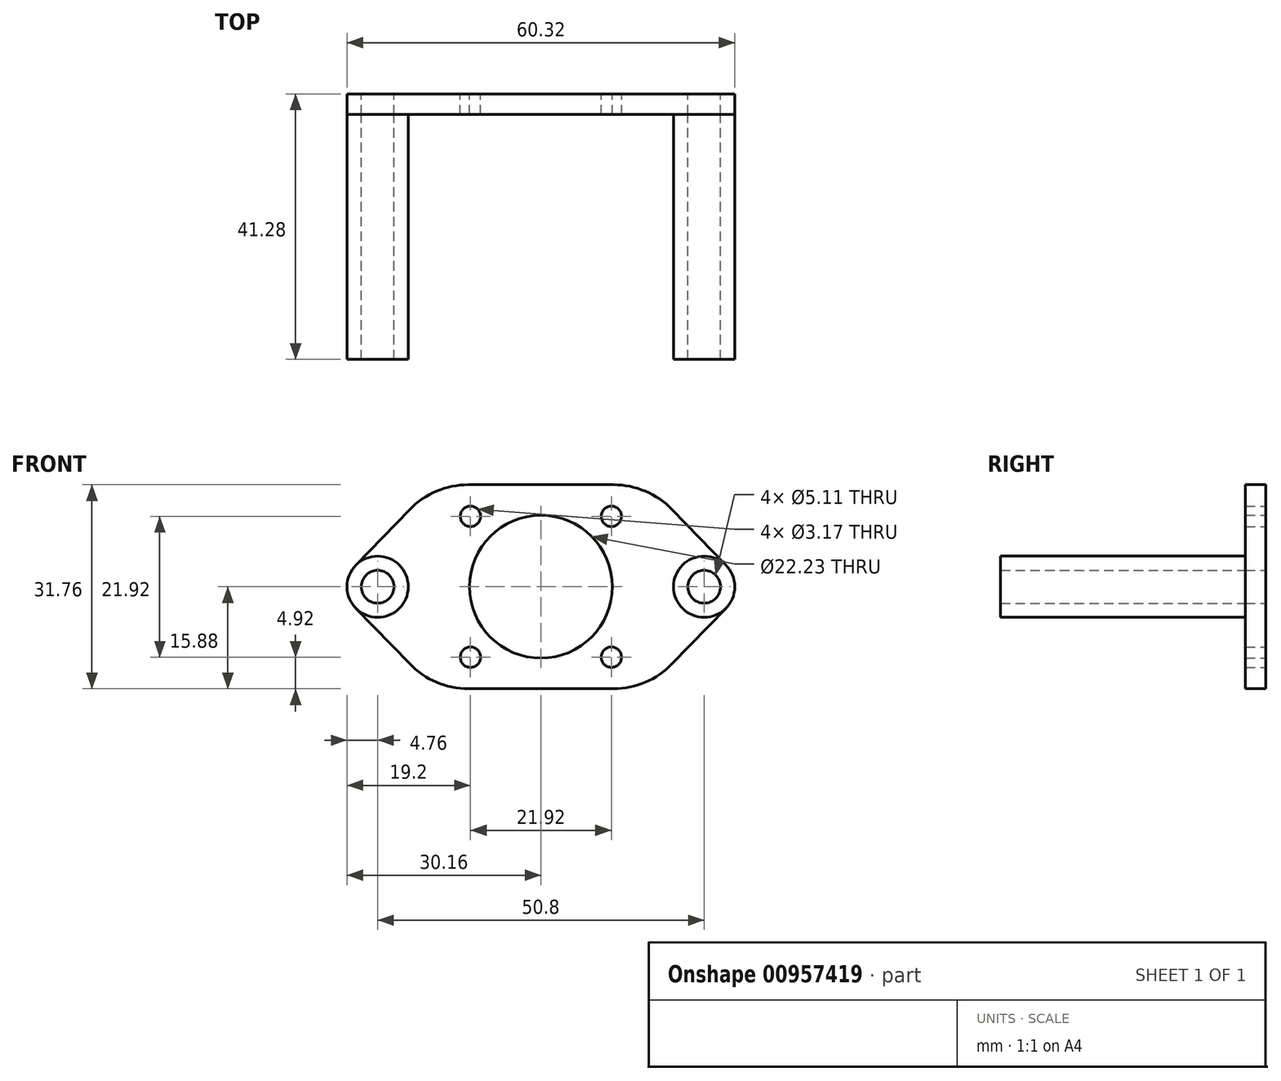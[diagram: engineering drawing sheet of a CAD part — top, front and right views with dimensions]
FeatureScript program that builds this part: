
annotation { "Feature Type Name" : "Feature", "Feature Type Description" : "" }
export const myFeature = defineFeature(function(context is Context, id is Id, definition is map)
    precondition{}
    {
        {
            var Q0;
            Q0=qCreatedBy(makeId("Front.planeOp"),FACE);
            var sketch = newSketch(context, id + "F0", { "sketchPlane" : qUnion([Q0])});
            skLineSegment(sketch, "E0", {"start": v(-25.4, 0) * mm, "end": v(0, 0) * mm, "construction": true});
            skLineSegment(sketch, "E1", {"start": v(25.4, 0) * mm, "end": v(0, 0) * mm, "construction": true});
            skCircle(sketch, "E2", {"center": v(-25.4, 0) * mm, "radius": 2.55 * mm});
            skCircle(sketch, "E3", {"center": v(25.4, 0) * mm, "radius": 2.55 * mm});
            skLineSegment(sketch, "E4.bottom", {"start": v(16.67, 15.88) * mm, "end": v(-16.67, 15.88) * mm, "construction": true});
            skLineSegment(sketch, "E4.top", {"start": v(16.67, -15.88) * mm, "end": v(-16.67, -15.88) * mm, "construction": true});
            skLineSegment(sketch, "E4.left", {"start": v(16.67, 15.88) * mm, "end": v(16.67, -15.88) * mm, "construction": true});
            skLineSegment(sketch, "E4.right", {"start": v(-16.67, 15.88) * mm, "end": v(-16.67, -15.88) * mm, "construction": true});
            skPoint(sketch, "E4.middle", {"position": v(0, 0) * mm});
            skLineSegment(sketch, "E5.bottom", {"start": v(10.96, 10.96) * mm, "end": v(-10.96, 10.96) * mm, "construction": true});
            skLineSegment(sketch, "E5.top", {"start": v(10.96, -10.96) * mm, "end": v(-10.96, -10.96) * mm, "construction": true});
            skLineSegment(sketch, "E5.left", {"start": v(10.96, 10.96) * mm, "end": v(10.96, -10.96) * mm, "construction": true});
            skLineSegment(sketch, "E5.right", {"start": v(-10.96, 10.96) * mm, "end": v(-10.96, -10.96) * mm, "construction": true});
            skCircle(sketch, "E6", {"center": v(10.96, 10.96) * mm, "radius": 1.59 * mm});
            skCircle(sketch, "E7", {"center": v(10.96, -10.96) * mm, "radius": 1.59 * mm});
            skCircle(sketch, "E8", {"center": v(-10.96, -10.96) * mm, "radius": 1.59 * mm});
            skCircle(sketch, "E9", {"center": v(-10.96, 10.96) * mm, "radius": 1.59 * mm});
            skArc(sketch, "E10", {"start": v(-28.82, 3.31) * mm, "mid": v(-30.16, 0) * mm, "end": v(-28.82, -3.31) * mm});
            skArc(sketch, "E11", {"start": v(28.82, 3.31) * mm, "mid": v(30.16, 0) * mm, "end": v(28.82, -3.31) * mm});
            skLineSegment(sketch, "E12", {"start": v(-28.82, 3.31) * mm, "end": v(-20.41, 12) * mm});
            skLineSegment(sketch, "E13", {"start": v(-28.82, -3.31) * mm, "end": v(-20.41, -12) * mm});
            skLineSegment(sketch, "E14", {"start": v(28.82, 3.31) * mm, "end": v(20.41, 12) * mm});
            skLineSegment(sketch, "E15", {"start": v(28.82, -3.31) * mm, "end": v(20.41, -12) * mm});
            skCircle(sketch, "E16", {"center": v(25.4, 0) * mm, "radius": 4.76 * mm, "construction": true});
            skCircle(sketch, "E17", {"center": v(-25.4, 0) * mm, "radius": 4.76 * mm, "construction": true});
            skLineSegment(sketch, "E18", {"start": v(-11.28, 15.88) * mm, "end": v(11.28, 15.88) * mm});
            skLineSegment(sketch, "E19", {"start": v(11.28, -15.88) * mm, "end": v(-11.28, -15.88) * mm});
            skPoint(sketch, "E20.visualSharp", {"position": v(-16.67, 15.88) * mm});
            skArc(sketch, "E20.filletArc", {"start": v(-11.28, 15.88) * mm, "mid": v(-16.24, 14.87) * mm, "end": v(-20.41, 12) * mm});
            skPoint(sketch, "E21.visualSharp", {"position": v(16.67, 15.88) * mm});
            skArc(sketch, "E21.filletArc", {"start": v(20.41, 12) * mm, "mid": v(16.24, 14.87) * mm, "end": v(11.28, 15.88) * mm});
            skPoint(sketch, "E22.visualSharp", {"position": v(16.67, -15.88) * mm});
            skArc(sketch, "E22.filletArc", {"start": v(11.28, -15.88) * mm, "mid": v(16.24, -14.87) * mm, "end": v(20.41, -12) * mm});
            skPoint(sketch, "E23.visualSharp", {"position": v(-16.67, -15.88) * mm});
            skArc(sketch, "E23.filletArc", {"start": v(-20.41, -12) * mm, "mid": v(-16.24, -14.87) * mm, "end": v(-11.28, -15.88) * mm});
            skCircle(sketch, "E24", {"center": v(0, 0) * mm, "radius": 11.11 * mm});
            skSolve(sketch);
        }
        {
            var Q0;
            Q0=makeQuery(id+"F0.imprint","IMPRINT",FACE,{"disambiguationData":[TD([[makeQuery(id+"F0.imprint","IMPRINT",EDGE,{"derivedFrom":sQuery(id+"F0.wireOp",EDGE,"E2")}),-1.0]])]});
            extrude(context, id + "F1", {"entities" : qUnion([Q0]), "depth" : 3.17 * mm, "offsetDistance" : 25.4 * mm});
        }
        {
            var Q0;
            Q0=makeQuery(id+"F1.opExtrude","CAP_FACE",FACE,{"disambiguationData":[OSD([sQuery(id+"F0.wireOp",EDGE,"E2"),sQuery(id+"F0.wireOp",EDGE,"E3"),sQuery(id+"F0.wireOp",EDGE,"E6"),sQuery(id+"F0.wireOp",EDGE,"E7"),sQuery(id+"F0.wireOp",EDGE,"E8"),sQuery(id+"F0.wireOp",EDGE,"E9"),sQuery(id+"F0.wireOp",EDGE,"E10"),sQuery(id+"F0.wireOp",EDGE,"E11"),sQuery(id+"F0.wireOp",EDGE,"E12"),sQuery(id+"F0.wireOp",EDGE,"E13"),sQuery(id+"F0.wireOp",EDGE,"E14"),sQuery(id+"F0.wireOp",EDGE,"E15"),sQuery(id+"F0.wireOp",EDGE,"E18"),sQuery(id+"F0.wireOp",EDGE,"E19"),sQuery(id+"F0.wireOp",EDGE,"E20.filletArc"),sQuery(id+"F0.wireOp",EDGE,"E21.filletArc"),sQuery(id+"F0.wireOp",EDGE,"E22.filletArc"),sQuery(id+"F0.wireOp",EDGE,"E23.filletArc"),sQuery(id+"F0.wireOp",EDGE,"E24")])],"isStart":false});
            var sketch = newSketch(context, id + "F2", { "sketchPlane" : qUnion([Q0])});
            skCircle(sketch, "E25", {"center": v(-25.4, 0) * mm, "radius": 4.76 * mm});
            skCircle(sketch, "E26", {"center": v(25.4, 0) * mm, "radius": 4.76 * mm});
            skCircle(sketch, "E27", {"center": v(-25.4, 0) * mm, "radius": 2.55 * mm});
            skCircle(sketch, "E28", {"center": v(25.4, 0) * mm, "radius": 2.55 * mm});
            skSolve(sketch);
        }
        {
            var Q0;
            Q0 = qSketchRegion(id + "F2", true);
            extrude(context, id + "F3", {"entities" : qUnion([Q0]), "depth" : 38.1 * mm, "offsetDistance" : 25.4 * mm});
        }
    });
